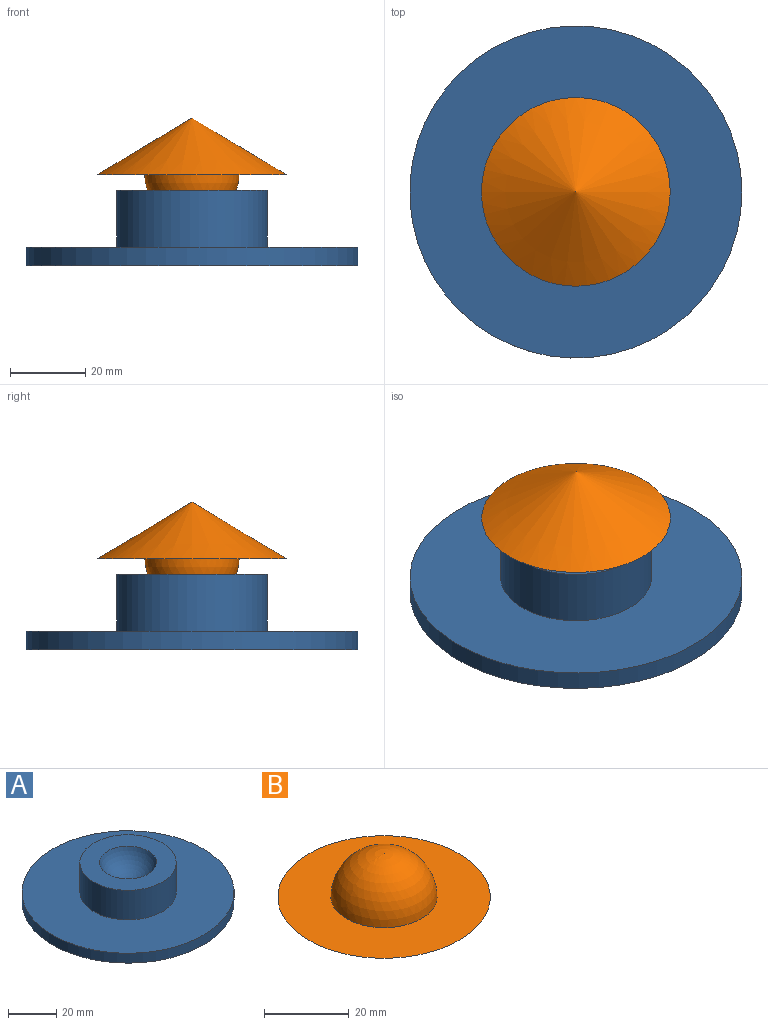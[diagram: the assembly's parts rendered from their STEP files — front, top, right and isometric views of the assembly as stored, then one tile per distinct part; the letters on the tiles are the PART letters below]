
ASSEMBLY  parts=2 mates=1
PART A: 8 faces, bbox 88x88x20 mm
  f0: plane 88x88mm, normal (0,0,1), area 4825.5mm2, adj f2,f5
  f1: cylinder r=42mm len=84mm, axis (0,0,1), area 791.7mm2, adj f3,f4
  f2: cylinder r=44mm len=88mm, axis (0,0,1), area 1382.3mm2, adj f0,f3
  f3: plane 88x88mm, normal (0,0,-1), area 540.4mm2, adj f1,f2
  f4: plane 84x84mm, normal (0,0,-1), area 5541.8mm2, adj f1
  f5: cylinder r=20mm len=40mm, axis (0,0,-1), area 1885mm2, adj f0,f6
  f6: plane 40x40mm, normal (0,0,1), area 821.3mm2, adj f5,f7
  f7: sphere r=12.5mm, area 651.6mm2, adj f6
PART B: 3 faces, bbox 50x50x27.5 mm
  f0: cone r=25mm half-angle=59deg, axis (0,0,1), area 2289.8mm2, adj f1
  f1: plane 50x50mm, normal (0,0,1), area 1472.6mm2, adj f0,f2
  f2: sphere r=12.5mm, area 981.7mm2, adj f1
PLACE A t=(-0.77,-15.49,-0.5)mm
PLACE B rot(axis=(0,1,0),180deg) t=(-0.77,-15.49,35.71)mm
MATE ball B.f0 <-> A.f2  axis (0,0,-1) through (-0.77,-15.49,20.71)mm
